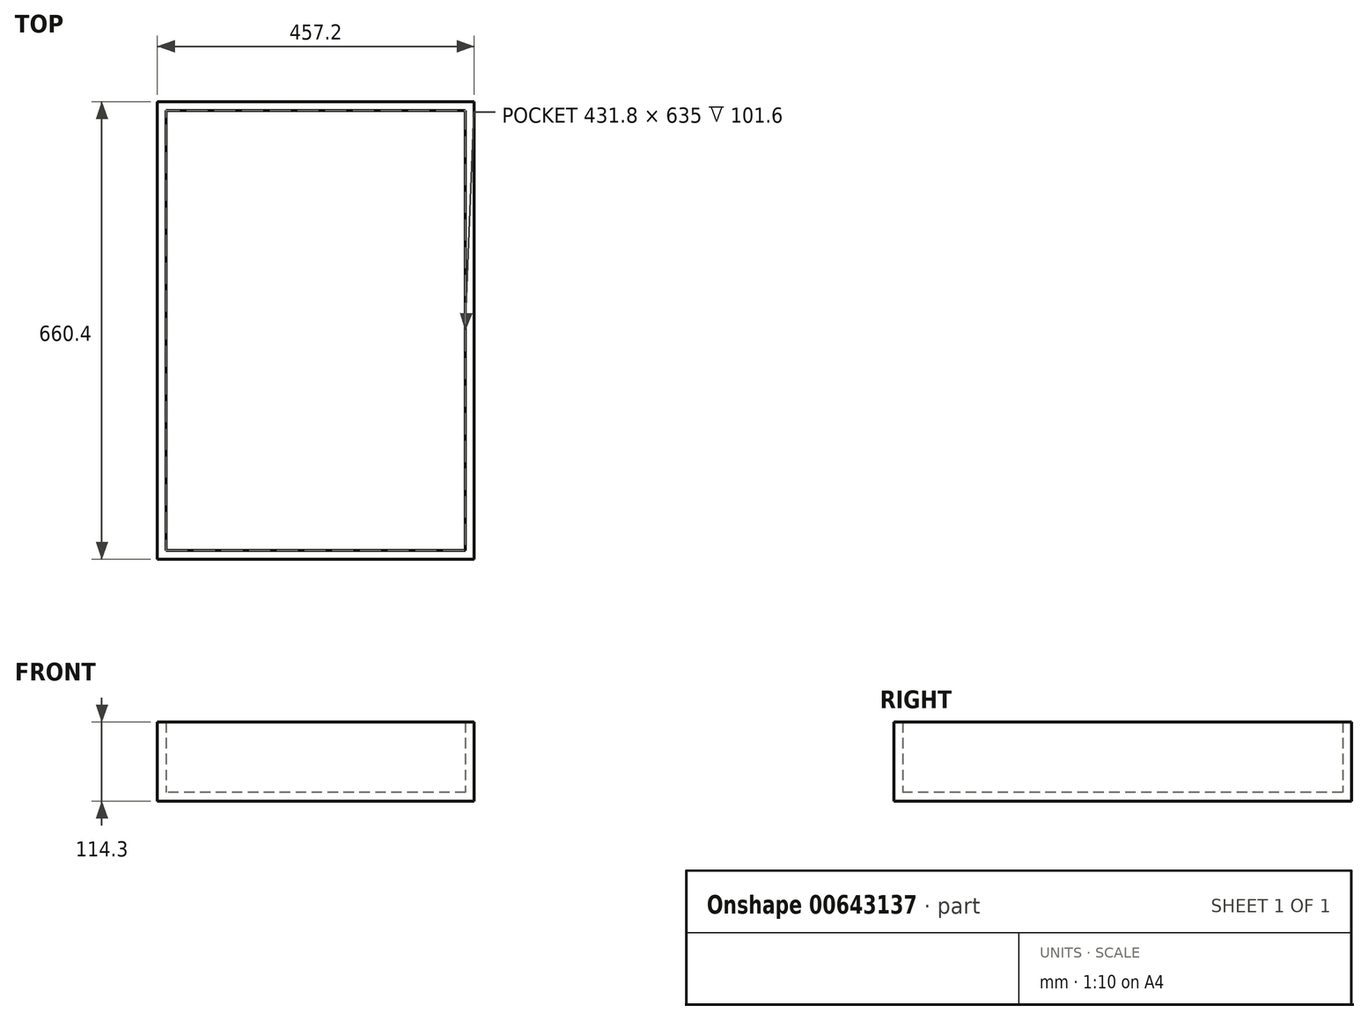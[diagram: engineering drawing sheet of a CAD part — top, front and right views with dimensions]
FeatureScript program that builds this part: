
annotation { "Feature Type Name" : "Feature", "Feature Type Description" : "" }
export const myFeature = defineFeature(function(context is Context, id is Id, definition is map)
    precondition{}
    {
        {
            var Q0;
            Q0=qCreatedBy(makeId("Top.planeOp"),FACE);
            var sketch = newSketch(context, id + "F0", { "sketchPlane" : qUnion([Q0])});
            skLineSegment(sketch, "E0.bottom", {"start": v(0, 0) * mm, "end": v(-457.2, 0) * mm});
            skLineSegment(sketch, "E0.top", {"start": v(0, 660.4) * mm, "end": v(-457.2, 660.4) * mm});
            skLineSegment(sketch, "E0.left", {"start": v(0, 0) * mm, "end": v(0, 660.4) * mm});
            skLineSegment(sketch, "E0.right", {"start": v(-457.2, 0) * mm, "end": v(-457.2, 660.4) * mm});
            skSolve(sketch);
        }
        {
            var Q0;
            Q0 = qSketchRegion(id + "F0", true);
            extrude(context, id + "F1", {"entities" : qUnion([Q0]), "depth" : 12.7 * mm, "offsetDistance" : 25.4 * mm});
        }
        {
            var Q0;
            Q0=makeQuery(id+"F1.opExtrude","CAP_FACE",FACE,{"disambiguationData":[OSD([sQuery(id+"F0.wireOp",EDGE,"E0.bottom"),sQuery(id+"F0.wireOp",EDGE,"E0.top"),sQuery(id+"F0.wireOp",EDGE,"E0.left"),sQuery(id+"F0.wireOp",EDGE,"E0.right")])],"isStart":false});
            var sketch = newSketch(context, id + "F2", { "sketchPlane" : qUnion([Q0])});
            skLineSegment(sketch, "E1.bottom", {"start": v(0, 660.4) * mm, "end": v(-12.7, 660.4) * mm});
            skLineSegment(sketch, "E1.top", {"start": v(0, 12.7) * mm, "end": v(-12.7, 12.7) * mm});
            skLineSegment(sketch, "E1.left", {"start": v(0, 660.4) * mm, "end": v(0, 12.7) * mm});
            skLineSegment(sketch, "E1.right", {"start": v(-12.7, 660.4) * mm, "end": v(-12.7, 12.7) * mm});
            skLineSegment(sketch, "E2.bottom", {"start": v(0, 0) * mm, "end": v(0, 0) * mm});
            skLineSegment(sketch, "E2.top", {"start": v(0, 12.7) * mm, "end": v(0, 12.7) * mm});
            skLineSegment(sketch, "E2.left", {"start": v(0, 0) * mm, "end": v(0, 12.7) * mm});
            skLineSegment(sketch, "E2.right", {"start": v(0, 0) * mm, "end": v(0, 12.7) * mm});
            skLineSegment(sketch, "E3.bottom", {"start": v(0, 0) * mm, "end": v(-444.5, 0) * mm});
            skLineSegment(sketch, "E3.top", {"start": v(0, 12.7) * mm, "end": v(-444.5, 12.7) * mm});
            skLineSegment(sketch, "E3.right", {"start": v(-444.5, 0) * mm, "end": v(-444.5, 12.7) * mm});
            skLineSegment(sketch, "E4.bottom", {"start": v(-444.5, 0) * mm, "end": v(-457.2, 0) * mm});
            skLineSegment(sketch, "E4.top", {"start": v(-444.5, 647.7) * mm, "end": v(-457.2, 647.7) * mm});
            skLineSegment(sketch, "E4.left", {"start": v(-444.5, 0) * mm, "end": v(-444.5, 647.7) * mm});
            skLineSegment(sketch, "E4.right", {"start": v(-457.2, 0) * mm, "end": v(-457.2, 647.7) * mm});
            skLineSegment(sketch, "E5.bottom", {"start": v(-457.2, 647.7) * mm, "end": v(-12.7, 647.7) * mm});
            skLineSegment(sketch, "E5.top", {"start": v(-457.2, 660.4) * mm, "end": v(-12.7, 660.4) * mm});
            skLineSegment(sketch, "E5.left", {"start": v(-457.2, 647.7) * mm, "end": v(-457.2, 660.4) * mm});
            skLineSegment(sketch, "E5.right", {"start": v(-12.7, 647.7) * mm, "end": v(-12.7, 660.4) * mm});
            skSolve(sketch);
        }
        {
            var Q0;
            Q0 = qSketchRegion(id + "F2", true);
            extrude(context, id + "F3", {"entities" : qUnion([Q0]), "operationType" : NewBodyOperationType.ADD, "depth" : 101.6 * mm, "offsetDistance" : 25.4 * mm});
        }
    });
